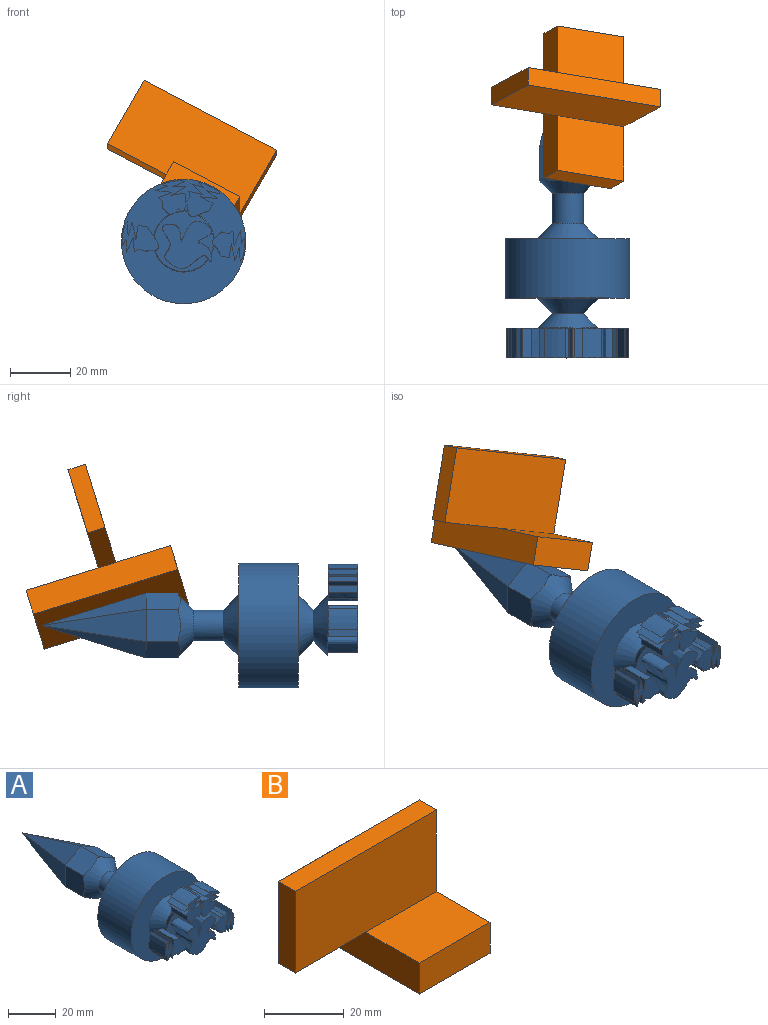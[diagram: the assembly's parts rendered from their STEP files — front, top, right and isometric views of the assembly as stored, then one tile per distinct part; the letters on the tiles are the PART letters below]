
ASSEMBLY  parts=2 mates=1
PART A: 96 faces, bbox 41.2x104.8x41.2 mm
  f0: plane 11.09x10.05mm, normal (0,-1,0), area 61.8mm2, adj f15,f16,f17,f18,f19,f20,f21,f22
  f1: plane 12.45x10.27mm, normal (0,-1,0), area 70.8mm2, adj f28,f29,f30,f31,f32,f33,f34,f35
  f2: plane 21.18x12.4mm, normal (0,-1,0), area 132.5mm2, adj f8,f9,f10,f11,f12,f13,f14,f41
  f3: plane 21.18x11.54mm, normal (0,1,0), area 128.4mm2, adj f6,f8,f9,f10,f11,f12,f13,f14
  f4: plane 10.7x10.05mm, normal (0,1,0), area 65.3mm2, adj f6,f28,f29,f30,f31,f32,f33,f34
  f5: plane 10.34x10.05mm, normal (0,1,0), area 60.7mm2, adj f6,f15,f16,f17,f18,f19,f20,f21
  f6: cone r=5.12mm half-angle=45deg, axis (0,-1,0), area 322.4mm2, adj f3,f4,f5,f48,f49,f80,f81,f82
  f7: plane 41.18x41.18mm, normal (0,-1,0), area 1010.1mm2, adj f62,f63
  f8: cylinder r=20.24mm len=9.77mm, axis (0,1,0), area 67.4mm2, adj f2,f3,f14,f50
  f9: plane 9.77x2.68mm, normal (0.87,0,-0.5), area 30.2mm2, adj f2,f3,f10,f85
  f10: plane 9.77x4.21mm, normal (0.45,0,0.9), area 45.9mm2, adj f2,f3,f9,f11
  f11: plane 9.77x5.62mm, normal (-0.1,0,-1), area 55.2mm2, adj f2,f3,f10,f12
  f12: plane 9.77x3.62mm, normal (0.59,0,0.81), area 43.7mm2, adj f2,f3,f11,f13
  f13: plane 9.77x4.37mm, normal (-0.24,0,-0.97), area 43.9mm2, adj f2,f3,f12,f14
  f14: plane 9.77x1.04mm, normal (0.83,0,0.55), area 12.1mm2, adj f2,f3,f8,f13
  f15: plane 9.77x2mm, normal (-0.87,0,0.49), area 22.5mm2, adj f0,f5,f16,f21
  f16: plane 9.77x4.25mm, normal (1,0,0.04), area 41.5mm2, adj f0,f5,f15,f17
  f17: plane 9.77x4.85mm, normal (-0.91,0,0.41), area 52mm2, adj f0,f5,f16,f18
  f18: plane 9.77x4.73mm, normal (1,0,0.08), area 46.4mm2, adj f0,f5,f17,f19
  f19: plane 9.77x1.53mm, normal (-0.54,0,0.84), area 17.7mm2, adj f0,f5,f18,f20
  f20: plane 9.77x2.26mm, normal (0.32,0,0.95), area 23.3mm2, adj f0,f5,f19,f86
  f21: cylinder r=20.24mm len=9.77mm, axis (0,1,0), area 67.4mm2, adj f0,f5,f15,f27
  f22: plane 9.77x3.03mm, normal (-0.21,0,-0.98), area 30.2mm2, adj f0,f5,f23,f86
  f23: plane 9.77x4.65mm, normal (0.99,0,-0.15), area 45.9mm2, adj f0,f5,f22,f24
  f24: plane 9.77x5.52mm, normal (-0.98,0,-0.22), area 55.2mm2, adj f0,f5,f23,f25
  f25: plane 9.77x4.25mm, normal (0.95,0,-0.31), area 43.7mm2, adj f0,f5,f24,f26
  f26: plane 9.77x4.49mm, normal (-1,0,-0.07), area 43.9mm2, adj f0,f5,f25,f27
  f27: plane 9.77x0.97mm, normal (0.78,0,-0.62), area 12.1mm2, adj f0,f5,f21,f26
  f28: plane 9.77x2mm, normal (0.87,0,-0.49), area 22.5mm2, adj f1,f4,f29,f34
  f29: plane 9.77x4.25mm, normal (-1,0,-0.04), area 41.5mm2, adj f1,f4,f28,f30
  f30: plane 9.77x4.85mm, normal (0.91,0,-0.41), area 52mm2, adj f1,f4,f29,f31
  f31: plane 9.77x4.73mm, normal (-1,0,-0.08), area 46.4mm2, adj f1,f4,f30,f32
  f32: plane 9.77x1.53mm, normal (0.54,0,-0.84), area 17.7mm2, adj f1,f4,f31,f33
  f33: plane 9.77x2.26mm, normal (-0.32,0,-0.95), area 23.3mm2, adj f1,f4,f32,f87
  f34: cylinder r=20.24mm len=9.77mm, axis (0,1,0), area 67.4mm2, adj f1,f4,f28,f40
  f35: plane 9.77x3.03mm, normal (0.21,0,0.98), area 30.2mm2, adj f1,f4,f36,f87
  f36: plane 9.77x4.65mm, normal (-0.99,0,0.15), area 45.9mm2, adj f1,f4,f35,f37
  f37: plane 9.77x5.52mm, normal (0.98,0,0.22), area 55.2mm2, adj f1,f4,f36,f38
  f38: plane 9.77x4.25mm, normal (-0.95,0,0.31), area 43.7mm2, adj f1,f4,f37,f39
  f39: plane 9.77x4.49mm, normal (1,0,0.07), area 43.9mm2, adj f1,f4,f38,f40
  f40: plane 9.77x0.97mm, normal (-0.78,0,0.62), area 12.1mm2, adj f1,f4,f34,f39
  f41: plane 9.77x2.25mm, normal (-0.2,0,-0.98), area 22.5mm2, adj f2,f3,f42,f47
  f42: plane 9.77x3.99mm, normal (-0.35,0,0.94), area 41.5mm2, adj f2,f3,f41,f43
  f43: plane 9.77x5.29mm, normal (-0.11,0,-0.99), area 52mm2, adj f2,f3,f42,f44
  f44: plane 9.77x4.39mm, normal (-0.38,0,0.92), area 46.4mm2, adj f2,f3,f43,f45
  f45: plane 9.77x1.39mm, normal (-0.64,0,-0.77), area 17.7mm2, adj f2,f3,f44,f46
  f46: plane 9.77x2.38mm, normal (-1,0,0.01), area 23.3mm2, adj f2,f3,f45,f88
  f47: cylinder r=20.24mm len=9.77mm, axis (0,1,0), area 67.4mm2, adj f2,f3,f41,f51
  f48: cylinder r=5.12mm len=10.24mm, axis (0,1,0), area 1.2mm2, adj f6,f62
  f49: plane 2.47x1.16mm, normal (0,1,0), area 1.2mm2, adj f6,f82
  f50: plane 9.77x1.7mm, normal (-0.74,0,-0.67), area 22.5mm2, adj f2,f3,f8,f52
  f51: plane 9.77x1.16mm, normal (0.35,0,0.94), area 12.1mm2, adj f2,f3,f47,f61
  f52: plane 9.77x4.09mm, normal (0.27,0,0.96), area 41.5mm2, adj f2,f3,f50,f53
  f53: plane 9.77x3.93mm, normal (-0.68,0,-0.74), area 52mm2, adj f2,f3,f52,f54
  f54: plane 9.77x4.61mm, normal (0.23,0,0.97), area 46.4mm2, adj f2,f3,f53,f55
  f55: plane 9.77x1.75mm, normal (-0.97,0,-0.25), area 17.7mm2, adj f2,f3,f54,f56
  f56: plane 9.77x1.92mm, normal (-0.8,0,0.6), area 23.3mm2, adj f2,f3,f55,f57
  f57: plane 9.77x3.08mm, normal (0.99,0,0.11), area 30.2mm2, adj f2,f3,f56,f58
  f58: plane 9.77x4.64mm, normal (-0.17,0,0.99), area 45.9mm2, adj f2,f3,f57,f59
  f59: plane 9.77x4.87mm, normal (0.51,0,-0.86), area 55.2mm2, adj f2,f3,f58,f60
  f60: plane 9.77x4.47mm, normal (0,0,1), area 43.7mm2, adj f2,f3,f59,f61
  f61: plane 9.77x4.16mm, normal (0.38,0,-0.93), area 43.9mm2, adj f2,f3,f51,f60
  f62: cone r=10.12mm half-angle=45deg, axis (0,1,0), area 338.5mm2, adj f7,f48
  f63: cylinder r=20.59mm len=41.18mm, axis (0,-1,0), area 2544.7mm2, adj f7,f79
  f64: plane 11.49x9.3mm, normal (0.5,0,0.87), area 118.9mm2, adj f65,f66,f74,f75,f76,f93
  f65: plane 2.42x0.7mm, normal (0,-1,0), area 0.7mm2, adj f64,f66,f76
  f66: plane 11.49x9.3mm, normal (-0.5,0,0.87), area 118.9mm2, adj f64,f65,f67,f68,f76,f94
  f67: plane 2.1x1.21mm, normal (0,-1,0), area 0.7mm2, adj f66,f68,f76
  f68: plane 11.49x10.74mm, normal (-1,0,0), area 118.9mm2, adj f66,f67,f69,f70,f76,f95
  f69: plane 2.1x1.21mm, normal (0,-1,0), area 0.7mm2, adj f68,f70,f76
  f70: plane 11.49x9.3mm, normal (-0.5,0,-0.87), area 118.9mm2, adj f68,f69,f71,f72,f76,f90
  f71: plane 2.42x0.7mm, normal (0,-1,0), area 0.7mm2, adj f70,f72,f76
  f72: plane 11.49x9.3mm, normal (0.5,0,-0.87), area 118.9mm2, adj f70,f71,f73,f74,f76,f91
  f73: plane 2.1x1.21mm, normal (0,-1,0), area 0.7mm2, adj f72,f74,f76
  f74: plane 11.49x10.74mm, normal (1,0,0), area 118.9mm2, adj f64,f72,f73,f75,f76,f92
  f75: plane 2.1x1.21mm, normal (0,-1,0), area 0.7mm2, adj f64,f74,f76
  f76: cone r=10.12mm half-angle=45deg, axis (0,1,0), area 301.6mm2, adj f64,f65,f66,f67,f68,f69,f70,f71
  f77: cylinder r=5.12mm len=10.24mm, axis (0,1,0), area 319.6mm2, adj f76,f78
  f78: cone r=5.12mm half-angle=45deg, axis (0,-1,0), area 338.5mm2, adj f77,f79
  f79: plane 41.18x41.18mm, normal (0,1,0), area 1010.1mm2, adj f63,f78
  f80: plane 19.77x19.03mm, normal (0,-1,0), area 117mm2, adj f6,f82,f83,f84,f85,f87,f88
  f81: plane 8.07x5.39mm, normal (0,-1,0), area 15.2mm2, adj f6,f82,f86
  f82: extruded ~16.07x15.57mm, area 739.7mm2, adj f6,f49,f80,f81,f89
  f83: plane 10x2.44mm, normal (0.86,0,-0.51), area 27.7mm2, adj f2,f3,f6,f80,f84,f85
  f84: plane 10x1.37mm, normal (-0.6,0,-0.8), area 16.7mm2, adj f2,f3,f6,f80,f83,f88
  f85: extruded ~10x7.07mm, area 103.5mm2, adj f2,f3,f6,f9,f80,f83
  f86: extruded ~10x7.99mm, area 100mm2, adj f0,f5,f6,f20,f22,f81
  f87: extruded ~10x7.99mm, area 124mm2, adj f1,f4,f6,f33,f35,f80
  f88: extruded ~10x5.33mm, area 65.9mm2, adj f2,f3,f6,f46,f80,f84
  f89: plane 16.96x16.33mm, normal (0,-1,0), area 168.9mm2, adj f82
  f90: plane 34.73x10.74mm, normal (-0.48,0.26,-0.84), area 193.1mm2, adj f70,f91,f95
  f91: plane 34.73x10.74mm, normal (0.48,0.26,-0.84), area 193.1mm2, adj f72,f90,f92
  f92: plane 34.73x10.74mm, normal (0.97,0.26,0), area 193.1mm2, adj f74,f91,f93
  f93: plane 34.73x10.74mm, normal (0.48,0.26,0.84), area 193.1mm2, adj f64,f92,f94
  f94: plane 34.73x10.74mm, normal (-0.48,0.26,0.84), area 193.1mm2, adj f66,f93,f95
  f95: plane 34.73x10.74mm, normal (-0.97,0.26,0), area 193.1mm2, adj f68,f90,f94
PART B: 12 faces, bbox 50x50x34.5 mm
  f0: plane 25x25mm, normal (0,0,1), area 625mm2, adj f4,f5,f6,f7
  f1: plane 25x18.94mm, normal (0,0,1), area 473.5mm2, adj f2,f5,f6,f9
  f2: plane 25x9.48mm, normal (0,-1,0), area 237mm2, adj f1,f3,f5,f6
  f3: plane 50x25mm, normal (0,0,-1), area 1250mm2, adj f2,f4,f5,f6
  f4: plane 25x9.48mm, normal (0,1,0), area 237mm2, adj f0,f3,f5,f6
  f5: plane 50x34.48mm, normal (1,0,0), area 625.5mm2, adj f0,f1,f2,f3,f4,f7,f9,f10
  f6: plane 50x9.48mm, normal (-1,0,0), area 474mm2, adj f0,f1,f2,f3,f4,f11
  f7: plane 50x25mm, normal (0,1,0), area 1250mm2, adj f0,f5,f8,f10,f11
  f8: plane 25x6.06mm, normal (-1,0,0), area 151.5mm2, adj f7,f9,f10,f11
  f9: plane 50x25mm, normal (0,-1,0), area 1250mm2, adj f1,f5,f8,f10,f11
  f10: plane 50x6.06mm, normal (0,0,1), area 303.1mm2, adj f5,f7,f8,f9
  f11: plane 25x6.06mm, normal (0,0,-1), area 151.5mm2, adj f6,f7,f8,f9
PLACE A t=(-35.8,-56.12,-31.38)mm
PLACE B rot(axis=(-0.5,0.86,-0.13),33.5deg) t=(-39.06,-109.76,-12.31)mm
MATE planar B.f3 <-> A.f93  axis (-0.48,-0.26,-0.84) through (-32.69,-114,-26)mm
